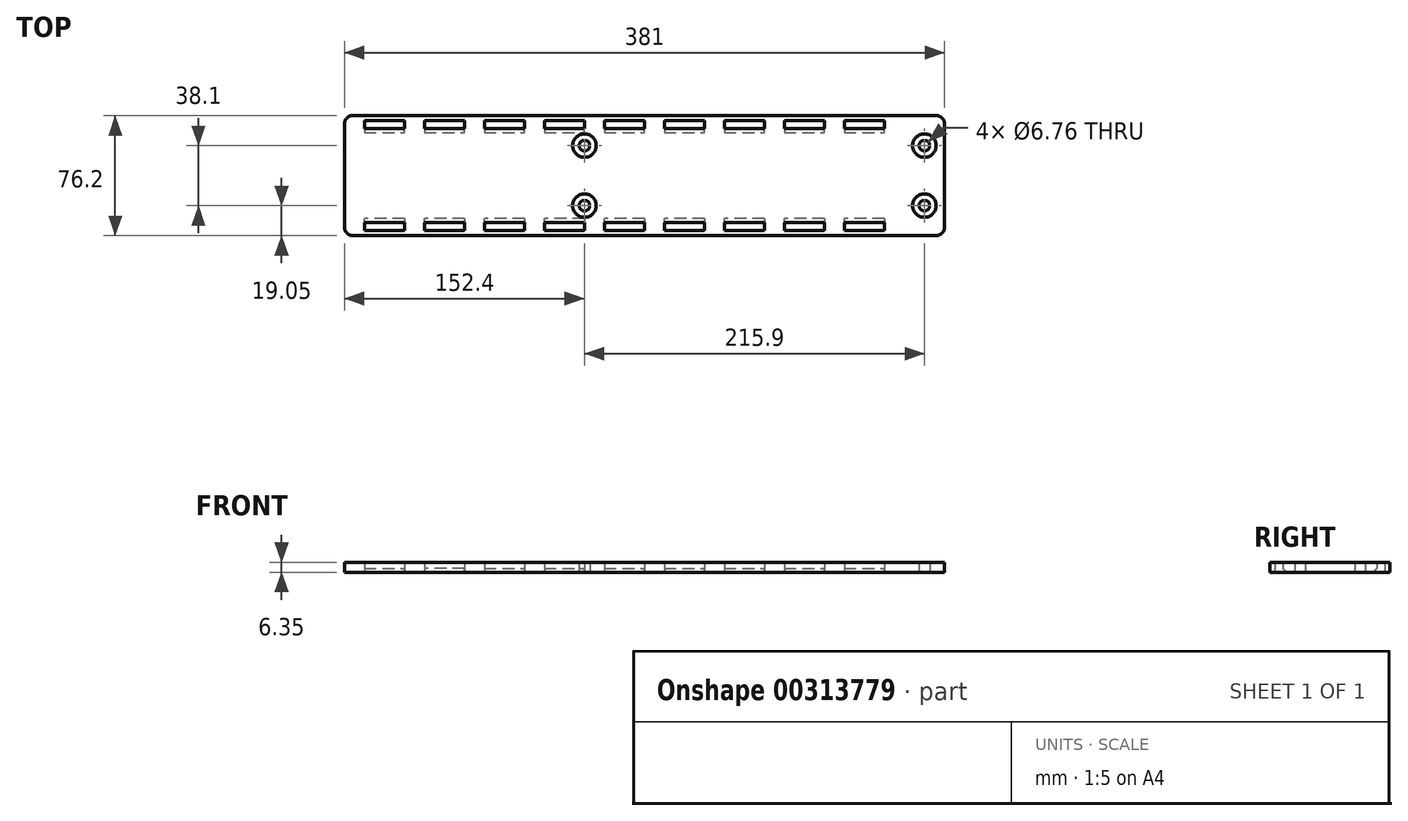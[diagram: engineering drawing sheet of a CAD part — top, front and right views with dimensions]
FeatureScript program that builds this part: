
annotation { "Feature Type Name" : "Feature", "Feature Type Description" : "" }
export const myFeature = defineFeature(function(context is Context, id is Id, definition is map)
    precondition{}
    {
        {
            var Q0;
            Q0=qCreatedBy(makeId("Top.planeOp"),FACE);
            var sketch = newSketch(context, id + "F0", { "sketchPlane" : qUnion([Q0])});
            skPoint(sketch, "E0.middle", {"position": v(0, 0) * mm});
            skCircle(sketch, "E1", {"center": v(-107.95, 19.05) * mm, "radius": 3.38 * mm});
            skCircle(sketch, "E2", {"center": v(107.95, 19.05) * mm, "radius": 3.38 * mm});
            skCircle(sketch, "E3.MirrorC", {"center": v(-107.95, -19.05) * mm, "radius": 3.38 * mm});
            skCircle(sketch, "E4.MirrorC", {"center": v(107.95, -19.05) * mm, "radius": 3.38 * mm});
            skLineSegment(sketch, "E5", {"start": v(120.65, 33.02) * mm, "end": v(120.65, -33.02) * mm});
            skLineSegment(sketch, "E6", {"start": v(-260.35, 33.02) * mm, "end": v(-260.35, -33.02) * mm});
            skLineSegment(sketch, "E7", {"start": v(-255.27, 38.1) * mm, "end": v(115.57, 38.1) * mm});
            skLineSegment(sketch, "E8", {"start": v(115.57, -38.1) * mm, "end": v(-255.27, -38.1) * mm});
            skLineSegment(sketch, "E9", {"start": v(-247.65, 34.92) * mm, "end": v(-247.65, 29.84) * mm});
            skLineSegment(sketch, "E10", {"start": v(-247.65, 29.84) * mm, "end": v(-222.25, 29.84) * mm});
            skLineSegment(sketch, "E11", {"start": v(-222.25, 29.84) * mm, "end": v(-222.25, 34.92) * mm});
            skLineSegment(sketch, "E12", {"start": v(-222.25, 34.92) * mm, "end": v(-247.65, 34.92) * mm});
            skLineSegment(sketch, "E13.1.0.0", {"start": v(-209.55, 29.84) * mm, "end": v(-184.15, 29.84) * mm});
            skLineSegment(sketch, "E13.1.0.1", {"start": v(-184.15, 34.92) * mm, "end": v(-209.55, 34.92) * mm});
            skLineSegment(sketch, "E13.1.0.2", {"start": v(-209.55, 34.92) * mm, "end": v(-209.55, 29.84) * mm});
            skLineSegment(sketch, "E13.1.0.3", {"start": v(-184.15, 29.84) * mm, "end": v(-184.15, 34.92) * mm});
            skLineSegment(sketch, "E13.2.0.0", {"start": v(-171.45, 29.84) * mm, "end": v(-146.05, 29.84) * mm});
            skLineSegment(sketch, "E13.2.0.1", {"start": v(-146.05, 34.92) * mm, "end": v(-171.45, 34.92) * mm});
            skLineSegment(sketch, "E13.2.0.2", {"start": v(-171.45, 34.92) * mm, "end": v(-171.45, 29.84) * mm});
            skLineSegment(sketch, "E13.2.0.3", {"start": v(-146.05, 29.84) * mm, "end": v(-146.05, 34.92) * mm});
            skLineSegment(sketch, "E13.3.0.0", {"start": v(-133.35, 29.85) * mm, "end": v(-107.95, 29.85) * mm});
            skLineSegment(sketch, "E13.3.0.1", {"start": v(-107.95, 34.93) * mm, "end": v(-133.35, 34.93) * mm});
            skLineSegment(sketch, "E13.3.0.2", {"start": v(-133.35, 34.92) * mm, "end": v(-133.35, 29.84) * mm});
            skLineSegment(sketch, "E13.3.0.3", {"start": v(-107.95, 29.84) * mm, "end": v(-107.95, 34.92) * mm});
            skLineSegment(sketch, "E13.4.0.0", {"start": v(-95.25, 29.85) * mm, "end": v(-69.85, 29.85) * mm});
            skLineSegment(sketch, "E13.4.0.1", {"start": v(-69.85, 34.93) * mm, "end": v(-95.25, 34.93) * mm});
            skLineSegment(sketch, "E13.4.0.2", {"start": v(-95.25, 34.92) * mm, "end": v(-95.25, 29.84) * mm});
            skLineSegment(sketch, "E13.4.0.3", {"start": v(-69.85, 29.84) * mm, "end": v(-69.85, 34.92) * mm});
            skLineSegment(sketch, "E13.5.0.0", {"start": v(-57.15, 29.85) * mm, "end": v(-31.75, 29.85) * mm});
            skLineSegment(sketch, "E13.5.0.1", {"start": v(-31.75, 34.93) * mm, "end": v(-57.15, 34.93) * mm});
            skLineSegment(sketch, "E13.5.0.2", {"start": v(-57.15, 34.92) * mm, "end": v(-57.15, 29.84) * mm});
            skLineSegment(sketch, "E13.5.0.3", {"start": v(-31.75, 29.84) * mm, "end": v(-31.75, 34.92) * mm});
            skLineSegment(sketch, "E13.6.0.0", {"start": v(-19.05, 29.85) * mm, "end": v(6.35, 29.85) * mm});
            skLineSegment(sketch, "E13.6.0.1", {"start": v(6.35, 34.93) * mm, "end": v(-19.05, 34.93) * mm});
            skLineSegment(sketch, "E13.6.0.2", {"start": v(-19.05, 34.92) * mm, "end": v(-19.05, 29.84) * mm});
            skLineSegment(sketch, "E13.6.0.3", {"start": v(6.35, 29.84) * mm, "end": v(6.35, 34.92) * mm});
            skLineSegment(sketch, "E13.7.0.0", {"start": v(19.05, 29.85) * mm, "end": v(44.45, 29.85) * mm});
            skLineSegment(sketch, "E13.7.0.1", {"start": v(44.45, 34.93) * mm, "end": v(19.05, 34.93) * mm});
            skLineSegment(sketch, "E13.7.0.2", {"start": v(19.05, 34.92) * mm, "end": v(19.05, 29.84) * mm});
            skLineSegment(sketch, "E13.7.0.3", {"start": v(44.45, 29.84) * mm, "end": v(44.45, 34.92) * mm});
            skLineSegment(sketch, "E13.8.0.0", {"start": v(57.15, 29.85) * mm, "end": v(82.55, 29.85) * mm});
            skLineSegment(sketch, "E13.8.0.1", {"start": v(82.55, 34.93) * mm, "end": v(57.15, 34.93) * mm});
            skLineSegment(sketch, "E13.8.0.2", {"start": v(57.15, 34.92) * mm, "end": v(57.15, 29.84) * mm});
            skLineSegment(sketch, "E13.8.0.3", {"start": v(82.55, 29.84) * mm, "end": v(82.55, 34.92) * mm});
            skLineSegment(sketch, "E13.direction1", {"start": v(-247.65, 29.84) * mm, "end": v(-209.55, 29.84) * mm, "construction": true});
            skLineSegment(sketch, "E14", {"start": v(-260.35, 0) * mm, "end": v(-149.28, 0) * mm});
            skPoint(sketch, "E14.endSnap0", {"position": v(-260.35, 0) * mm});
            skLineSegment(sketch, "E15.MirrorCS", {"start": v(-19.05, -34.92) * mm, "end": v(-19.05, -29.84) * mm});
            skLineSegment(sketch, "E16.MirrorCS", {"start": v(57.15, -34.92) * mm, "end": v(57.15, -29.84) * mm});
            skLineSegment(sketch, "E17.MirrorCS", {"start": v(-95.25, -34.92) * mm, "end": v(-95.25, -29.84) * mm});
            skLineSegment(sketch, "E18.MirrorCS", {"start": v(-146.05, -29.84) * mm, "end": v(-146.05, -34.92) * mm});
            skLineSegment(sketch, "E19.MirrorCS", {"start": v(6.35, -29.84) * mm, "end": v(6.35, -34.92) * mm});
            skLineSegment(sketch, "E20.MirrorCS", {"start": v(-209.55, -34.92) * mm, "end": v(-209.55, -29.84) * mm});
            skLineSegment(sketch, "E21.MirrorCS", {"start": v(-184.15, -29.84) * mm, "end": v(-184.15, -34.92) * mm});
            skLineSegment(sketch, "E22.MirrorCS", {"start": v(-31.75, -29.84) * mm, "end": v(-31.75, -34.92) * mm});
            skLineSegment(sketch, "E23.MirrorCS", {"start": v(-247.65, -34.92) * mm, "end": v(-247.65, -29.84) * mm});
            skLineSegment(sketch, "E24.MirrorCS", {"start": v(-69.85, -29.84) * mm, "end": v(-69.85, -34.92) * mm});
            skLineSegment(sketch, "E25.MirrorCS", {"start": v(82.55, -29.84) * mm, "end": v(82.55, -34.92) * mm});
            skLineSegment(sketch, "E26.MirrorCS", {"start": v(44.45, -29.84) * mm, "end": v(44.45, -34.92) * mm});
            skLineSegment(sketch, "E27.MirrorCS", {"start": v(-171.45, -34.92) * mm, "end": v(-171.45, -29.84) * mm});
            skLineSegment(sketch, "E28.MirrorCS", {"start": v(-133.35, -34.92) * mm, "end": v(-133.35, -29.84) * mm});
            skLineSegment(sketch, "E29.MirrorCS", {"start": v(19.05, -34.92) * mm, "end": v(19.05, -29.84) * mm});
            skLineSegment(sketch, "E30.MirrorCS", {"start": v(-107.95, -29.84) * mm, "end": v(-107.95, -34.92) * mm});
            skLineSegment(sketch, "E31.MirrorCS", {"start": v(-222.25, -29.84) * mm, "end": v(-222.25, -34.92) * mm});
            skLineSegment(sketch, "E32.MirrorCS", {"start": v(-57.15, -34.92) * mm, "end": v(-57.15, -29.84) * mm});
            skLineSegment(sketch, "E33.MirrorCS", {"start": v(-247.65, -29.84) * mm, "end": v(-222.25, -29.84) * mm});
            skLineSegment(sketch, "E34.MirrorCS", {"start": v(-184.15, -34.92) * mm, "end": v(-209.55, -34.92) * mm});
            skLineSegment(sketch, "E35.MirrorCS", {"start": v(-209.55, -29.84) * mm, "end": v(-184.15, -29.84) * mm});
            skLineSegment(sketch, "E36.MirrorCS", {"start": v(-133.35, -29.84) * mm, "end": v(-107.95, -29.84) * mm});
            skLineSegment(sketch, "E37.MirrorCS", {"start": v(19.05, -29.84) * mm, "end": v(44.45, -29.84) * mm});
            skLineSegment(sketch, "E38.MirrorCS", {"start": v(-222.25, -34.92) * mm, "end": v(-247.65, -34.92) * mm});
            skLineSegment(sketch, "E39.MirrorCS", {"start": v(6.35, -34.92) * mm, "end": v(-19.05, -34.92) * mm});
            skLineSegment(sketch, "E40.MirrorCS", {"start": v(-146.05, -34.92) * mm, "end": v(-171.45, -34.92) * mm});
            skLineSegment(sketch, "E41.MirrorCS", {"start": v(-107.95, -34.92) * mm, "end": v(-133.35, -34.92) * mm});
            skLineSegment(sketch, "E42.MirrorCS", {"start": v(57.15, -29.84) * mm, "end": v(82.55, -29.84) * mm});
            skLineSegment(sketch, "E43.MirrorCS", {"start": v(82.55, -34.92) * mm, "end": v(57.15, -34.92) * mm});
            skLineSegment(sketch, "E44.MirrorCS", {"start": v(-69.85, -34.92) * mm, "end": v(-95.25, -34.92) * mm});
            skLineSegment(sketch, "E45.MirrorCS", {"start": v(-171.45, -29.84) * mm, "end": v(-146.05, -29.84) * mm});
            skLineSegment(sketch, "E46.MirrorCS", {"start": v(-31.75, -34.92) * mm, "end": v(-57.15, -34.92) * mm});
            skLineSegment(sketch, "E47.MirrorCS", {"start": v(-19.05, -29.84) * mm, "end": v(6.35, -29.84) * mm});
            skLineSegment(sketch, "E48.MirrorCS", {"start": v(-247.65, -29.84) * mm, "end": v(-209.55, -29.84) * mm, "construction": true});
            skLineSegment(sketch, "E49.MirrorCS", {"start": v(-57.15, -29.84) * mm, "end": v(-31.75, -29.84) * mm});
            skLineSegment(sketch, "E50.MirrorCS", {"start": v(-95.25, -29.84) * mm, "end": v(-69.85, -29.84) * mm});
            skLineSegment(sketch, "E51.MirrorCS", {"start": v(44.45, -34.92) * mm, "end": v(19.05, -34.92) * mm});
            skPoint(sketch, "E52.visualSharp", {"position": v(-260.35, 38.1) * mm});
            skArc(sketch, "E52.filletArc", {"start": v(-255.27, 38.1) * mm, "mid": v(-258.86, 36.61) * mm, "end": v(-260.35, 33.02) * mm});
            skPoint(sketch, "E53.visualSharp", {"position": v(-260.35, -38.1) * mm});
            skArc(sketch, "E53.filletArc", {"start": v(-260.35, -33.02) * mm, "mid": v(-258.86, -36.61) * mm, "end": v(-255.27, -38.1) * mm});
            skPoint(sketch, "E54.visualSharp", {"position": v(120.65, -38.1) * mm});
            skArc(sketch, "E54.filletArc", {"start": v(115.57, -38.1) * mm, "mid": v(119.16, -36.61) * mm, "end": v(120.65, -33.02) * mm});
            skPoint(sketch, "E55.visualSharp", {"position": v(120.65, 38.1) * mm});
            skArc(sketch, "E55.filletArc", {"start": v(120.65, 33.02) * mm, "mid": v(119.16, 36.61) * mm, "end": v(115.57, 38.1) * mm});
            skSolve(sketch);
        }
        {
            var Q0;
            Q0=makeQuery(id+"F0.imprint","IMPRINT",FACE,{"disambiguationData":[TD([[makeQuery(id+"F0.imprint","IMPRINT",EDGE,{"derivedFrom":sQuery(id+"F0.wireOp",EDGE,"E1")}),-1.0]])]});
            var Q1;
            {var subQ2=sQuery(id+"F0.wireOp",EDGE,"E0.top");Q1=makeQuery(id+"F0.imprint","IMPRINT",FACE,{"disambiguationData":[TD([[makeQuery(id+"F0.imprint","IMPRINT",EDGE,{"derivedFrom":subQ2}),-1.0]])]});}
            extrude(context, id + "F1", {"entities" : qUnion([Q0, Q1]), "depth" : 6.35 * mm});
        }
        {
            var Q0;
            Q0=makeQuery(id+"F1.opExtrude","CAP_EDGE",EDGE,{"disambiguationData":[OSD([sQuery(id+"F0.wireOp",EDGE,"E33.MirrorCS")])],"isStart":true});
            var Q1;
            Q1=makeQuery(id+"F1.opExtrude","CAP_EDGE",EDGE,{"disambiguationData":[OSD([sQuery(id+"F0.wireOp",EDGE,"E35.MirrorCS")])],"isStart":true});
            var Q2;
            Q2=makeQuery(id+"F1.opExtrude","CAP_EDGE",EDGE,{"disambiguationData":[OSD([sQuery(id+"F0.wireOp",EDGE,"E45.MirrorCS")])],"isStart":true});
            var Q3;
            Q3=makeQuery(id+"F1.opExtrude","CAP_EDGE",EDGE,{"disambiguationData":[OSD([sQuery(id+"F0.wireOp",EDGE,"E36.MirrorCS")])],"isStart":true});
            var Q4;
            Q4=makeQuery(id+"F1.opExtrude","CAP_EDGE",EDGE,{"disambiguationData":[OSD([sQuery(id+"F0.wireOp",EDGE,"E50.MirrorCS")])],"isStart":true});
            var Q5;
            Q5=makeQuery(id+"F1.opExtrude","CAP_EDGE",EDGE,{"disambiguationData":[OSD([sQuery(id+"F0.wireOp",EDGE,"E49.MirrorCS")])],"isStart":true});
            var Q6;
            Q6=makeQuery(id+"F1.opExtrude","CAP_EDGE",EDGE,{"disambiguationData":[OSD([sQuery(id+"F0.wireOp",EDGE,"E47.MirrorCS")])],"isStart":true});
            var Q7;
            Q7=makeQuery(id+"F1.opExtrude","CAP_EDGE",EDGE,{"disambiguationData":[OSD([sQuery(id+"F0.wireOp",EDGE,"E37.MirrorCS")])],"isStart":true});
            var Q8;
            Q8=makeQuery(id+"F1.opExtrude","CAP_EDGE",EDGE,{"disambiguationData":[OSD([sQuery(id+"F0.wireOp",EDGE,"E42.MirrorCS")])],"isStart":true});
            var Q9;
            Q9=makeQuery(id+"F1.opExtrude","CAP_EDGE",EDGE,{"disambiguationData":[OSD([sQuery(id+"F0.wireOp",EDGE,"E13.8.0.0")])],"isStart":true});
            var Q10;
            Q10=makeQuery(id+"F1.opExtrude","CAP_EDGE",EDGE,{"disambiguationData":[OSD([sQuery(id+"F0.wireOp",EDGE,"E13.7.0.0")])],"isStart":true});
            var Q11;
            Q11=makeQuery(id+"F1.opExtrude","CAP_EDGE",EDGE,{"disambiguationData":[OSD([sQuery(id+"F0.wireOp",EDGE,"E13.6.0.0")])],"isStart":true});
            var Q12;
            Q12=makeQuery(id+"F1.opExtrude","CAP_EDGE",EDGE,{"disambiguationData":[OSD([sQuery(id+"F0.wireOp",EDGE,"E13.5.0.0")])],"isStart":true});
            var Q13;
            Q13=makeQuery(id+"F1.opExtrude","CAP_EDGE",EDGE,{"disambiguationData":[OSD([sQuery(id+"F0.wireOp",EDGE,"E13.4.0.0")])],"isStart":true});
            var Q14;
            Q14=makeQuery(id+"F1.opExtrude","CAP_EDGE",EDGE,{"disambiguationData":[OSD([sQuery(id+"F0.wireOp",EDGE,"E13.3.0.0")])],"isStart":true});
            var Q15;
            Q15=makeQuery(id+"F1.opExtrude","CAP_EDGE",EDGE,{"disambiguationData":[OSD([sQuery(id+"F0.wireOp",EDGE,"E13.2.0.0")])],"isStart":true});
            var Q16;
            Q16=makeQuery(id+"F1.opExtrude","CAP_EDGE",EDGE,{"disambiguationData":[OSD([sQuery(id+"F0.wireOp",EDGE,"E13.1.0.0")])],"isStart":true});
            var Q17;
            Q17=makeQuery(id+"F1.opExtrude","CAP_EDGE",EDGE,{"disambiguationData":[OSD([sQuery(id+"F0.wireOp",EDGE,"E10")])],"isStart":true});
            chamfer(context, id + "F2", {"entities" : qUnion([Q0, Q1, Q2, Q3, Q4, Q5, Q6, Q7, Q8, Q9, Q10, Q11, Q12, Q13, Q14, Q15, Q16, Q17]), "width" : 2.54 * mm, "tangentPropagation" : true});
        }
        {
            var Q0;
            Q0=makeQuery(id+"F1.opExtrude","CAP_EDGE",EDGE,{"disambiguationData":[OSD([sQuery(id+"F0.wireOp",EDGE,"E3.MirrorC")])],"isStart":false});
            var Q1;
            Q1=makeQuery(id+"F1.opExtrude","CAP_EDGE",EDGE,{"disambiguationData":[OSD([sQuery(id+"F0.wireOp",EDGE,"E1")])],"isStart":false});
            var Q2;
            Q2=makeQuery(id+"F1.opExtrude","CAP_EDGE",EDGE,{"disambiguationData":[OSD([sQuery(id+"F0.wireOp",EDGE,"E4.MirrorC")])],"isStart":false});
            var Q3;
            Q3=makeQuery(id+"F1.opExtrude","CAP_EDGE",EDGE,{"disambiguationData":[OSD([sQuery(id+"F0.wireOp",EDGE,"E2")])],"isStart":false});
            chamfer(context, id + "F3", {"entities" : qUnion([Q0, Q1, Q2, Q3]), "chamferType" : ChamferType.TWO_OFFSETS, "width1" : ((.531 - .266) / 2) * mm, "oppositeDirection" : false, "width2" : 4.1 * mm, "tangentPropagation" : true});
        }
    });
